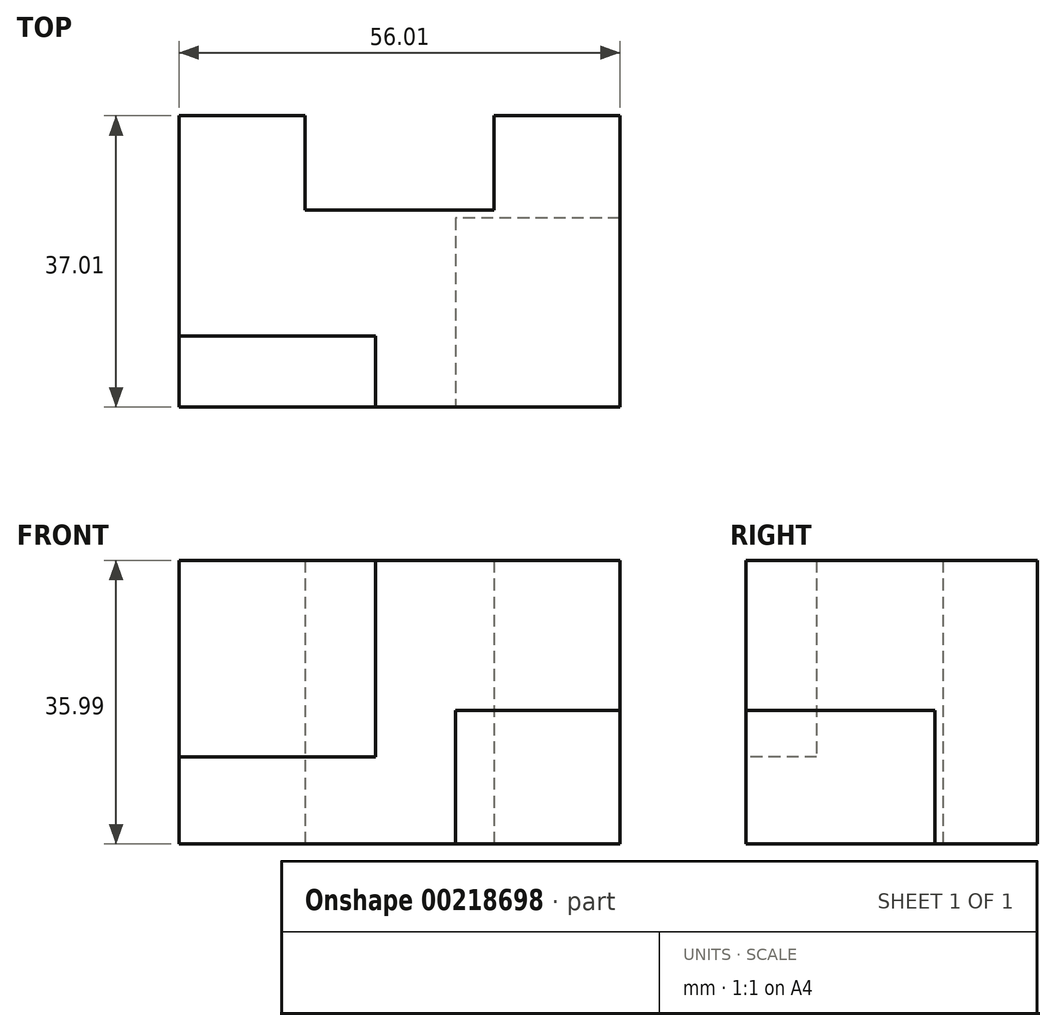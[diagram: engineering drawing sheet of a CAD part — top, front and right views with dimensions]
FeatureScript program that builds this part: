
annotation { "Feature Type Name" : "Feature", "Feature Type Description" : "" }
export const myFeature = defineFeature(function(context is Context, id is Id, definition is map)
    precondition{}
    {
        {
            var Q0;
            Q0=qCreatedBy(makeId("Top.planeOp"),FACE);
            var sketch = newSketch(context, id + "F0", { "sketchPlane" : qUnion([Q0])});
            skLineSegment(sketch, "E0.bottom", {"start": v(0, 0) * mm, "end": v(-16, 0) * mm});
            skLineSegment(sketch, "E0.top", {"start": v(0, -37) * mm, "end": v(-56, -37) * mm});
            skLineSegment(sketch, "E0.left", {"start": v(0, 0) * mm, "end": v(0, -37) * mm});
            skLineSegment(sketch, "E0.right", {"start": v(-56, 0) * mm, "end": v(-56, -37) * mm});
            skLineSegment(sketch, "E1.0", {"start": v(-40, 0) * mm, "end": v(-40, -11.99) * mm});
            skLineSegment(sketch, "E2.0", {"start": v(-16, 0) * mm, "end": v(-16, -11.99) * mm});
            skLineSegment(sketch, "E3.0", {"start": v(-16, -11.99) * mm, "end": v(-40, -11.99) * mm});
            skLineSegment(sketch, "E4.trimOffspring", {"start": v(-40, 0) * mm, "end": v(-56, 0) * mm});
            skSolve(sketch);
        }
        {
            var Q0;
            Q0=makeQuery(id+"F0.imprint","IMPRINT",FACE,{"disambiguationData":[TD([[makeQuery(id+"F0.imprint","IMPRINT",EDGE,{"derivedFrom":sQuery(id+"F0.wireOp",EDGE,"E0.bottom")}),1.0]])]});
            extrude(context, id + "F1", {"entities" : qUnion([Q0]), "depth" : 36 * mm});
        }
        {
            var Q0;
            Q0=makeQuery(id+"F1.opExtrude","SWEPT_FACE",FACE,{"disambiguationData":[OSD([sQuery(id+"F0.wireOp",EDGE,"E0.top")])]});
            var sketch = newSketch(context, id + "F2", { "sketchPlane" : qUnion([Q0])});
            skLineSegment(sketch, "E5.bottom", {"start": v(-56, 36) * mm, "end": v(-31.04, 36) * mm});
            skLineSegment(sketch, "E5.top", {"start": v(-56, 11.05) * mm, "end": v(-31.04, 11.05) * mm});
            skLineSegment(sketch, "E5.left", {"start": v(-56, 36) * mm, "end": v(-56, 11.05) * mm});
            skLineSegment(sketch, "E5.right", {"start": v(-31.04, 36) * mm, "end": v(-31.04, 11.05) * mm});
            skSolve(sketch);
        }
        {
            var Q0;
            Q0=makeQuery(id+"F2.imprint","IMPRINT",FACE,{"disambiguationData":[TD([[makeQuery(id+"F2.imprint","IMPRINT",EDGE,{"derivedFrom":sQuery(id+"F2.wireOp",EDGE,"E5.bottom")}),1.0]])]});
            extrude(context, id + "F3", {"entities" : qUnion([Q0]), "operationType" : NewBodyOperationType.REMOVE, "oppositeDirection" : true, "depth" : 9 * mm});
        }
        {
            var Q0;
            Q0=makeQuery(id+"F1.opExtrude","SWEPT_FACE",FACE,{"disambiguationData":[OSD([sQuery(id+"F0.wireOp",EDGE,"E0.top")])]});
            var sketch = newSketch(context, id + "F4", { "sketchPlane" : qUnion([Q0])});
            skLineSegment(sketch, "E6.bottom", {"start": v(0, 0) * mm, "end": v(-20.85, 0) * mm});
            skLineSegment(sketch, "E6.top", {"start": v(0, 16.94) * mm, "end": v(-20.85, 16.94) * mm});
            skLineSegment(sketch, "E6.left", {"start": v(0, 0) * mm, "end": v(0, 16.94) * mm});
            skLineSegment(sketch, "E6.right", {"start": v(-20.85, 0) * mm, "end": v(-20.85, 16.94) * mm});
            skSolve(sketch);
        }
        {
            var Q0;
            Q0=makeQuery(id+"F4.imprint","IMPRINT",FACE,{"disambiguationData":[TD([[makeQuery(id+"F4.imprint","IMPRINT",EDGE,{"derivedFrom":sQuery(id+"F4.wireOp",EDGE,"E6.bottom")}),-1.0]])]});
            extrude(context, id + "F5", {"entities" : qUnion([Q0]), "operationType" : NewBodyOperationType.REMOVE, "oppositeDirection" : true, "depth" : 24 * mm});
        }
    });
